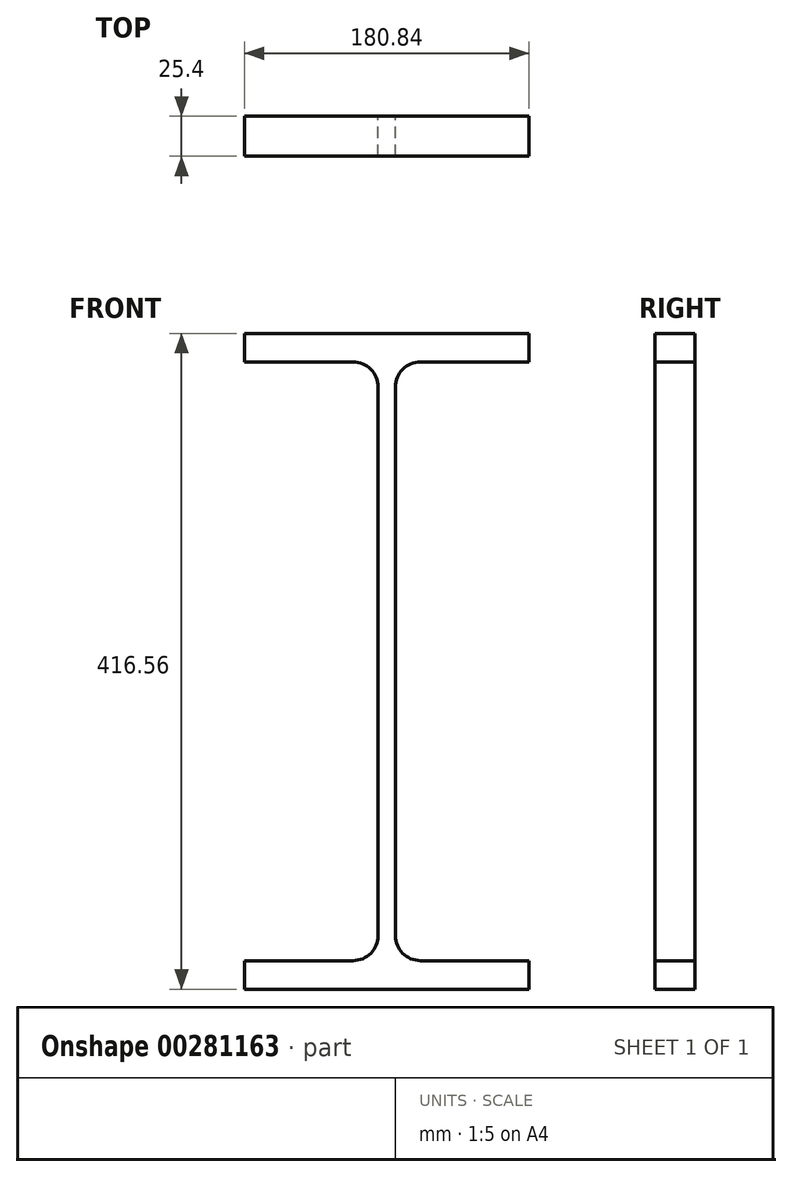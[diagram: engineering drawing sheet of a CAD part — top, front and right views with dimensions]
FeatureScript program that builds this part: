
annotation { "Feature Type Name" : "Feature", "Feature Type Description" : "" }
export const myFeature = defineFeature(function(context is Context, id is Id, definition is map)
    precondition{}
    {
        {
            var Q0;
            Q0=qCreatedBy(makeId("Front.planeOp"),FACE);
            var sketch = newSketch(context, id + "F0", { "sketchPlane" : qUnion([Q0])});
            skLineSegment(sketch, "E0.bottom", {"start": v(-90.42, 208.28) * mm, "end": v(90.42, 208.28) * mm});
            skLineSegment(sketch, "E0.top", {"start": v(-90.42, -208.28) * mm, "end": v(90.42, -208.28) * mm});
            skLineSegment(sketch, "E0.left", {"start": v(-90.42, 208.28) * mm, "end": v(-90.42, -208.28) * mm, "construction": true});
            skLineSegment(sketch, "E0.right", {"start": v(90.42, 208.28) * mm, "end": v(90.42, -208.28) * mm, "construction": true});
            skPoint(sketch, "E0.middle", {"position": v(0, 0) * mm});
            skLineSegment(sketch, "E1", {"start": v(-90.42, 208.28) * mm, "end": v(-90.42, 190.12) * mm});
            skLineSegment(sketch, "E2", {"start": v(-90.42, 190.12) * mm, "end": v(-21.34, 190.12) * mm});
            skLineSegment(sketch, "E3", {"start": v(-5.46, 174.24) * mm, "end": v(-5.46, -174.24) * mm});
            skLineSegment(sketch, "E4", {"start": v(-21.34, -190.12) * mm, "end": v(-90.42, -190.12) * mm});
            skLineSegment(sketch, "E5", {"start": v(-90.42, -190.12) * mm, "end": v(-90.42, -208.28) * mm});
            skLineSegment(sketch, "E6", {"start": v(90.42, 208.28) * mm, "end": v(90.42, 190.12) * mm});
            skLineSegment(sketch, "E7", {"start": v(90.42, 190.12) * mm, "end": v(21.34, 190.12) * mm});
            skLineSegment(sketch, "E8", {"start": v(5.46, 174.24) * mm, "end": v(5.46, -174.24) * mm});
            skLineSegment(sketch, "E9", {"start": v(21.34, -190.12) * mm, "end": v(90.42, -190.12) * mm});
            skLineSegment(sketch, "E10", {"start": v(90.42, -190.12) * mm, "end": v(90.42, -208.28) * mm});
            skPoint(sketch, "E11.visualSharp", {"position": v(-5.46, 190.12) * mm});
            skArc(sketch, "E11.filletArc", {"start": v(-5.46, 174.24) * mm, "mid": v(-10.11, 185.47) * mm, "end": v(-21.34, 190.12) * mm});
            skPoint(sketch, "E12.visualSharp", {"position": v(5.46, 190.12) * mm});
            skArc(sketch, "E12.filletArc", {"start": v(21.34, 190.12) * mm, "mid": v(10.11, 185.47) * mm, "end": v(5.46, 174.24) * mm});
            skPoint(sketch, "E13.visualSharp", {"position": v(5.46, -190.12) * mm});
            skArc(sketch, "E13.filletArc", {"start": v(5.46, -174.24) * mm, "mid": v(10.11, -185.47) * mm, "end": v(21.34, -190.12) * mm});
            skPoint(sketch, "E14.visualSharp", {"position": v(-5.46, -190.12) * mm});
            skArc(sketch, "E14.filletArc", {"start": v(-21.34, -190.12) * mm, "mid": v(-10.11, -185.47) * mm, "end": v(-5.46, -174.24) * mm});
            skSolve(sketch);
        }
        {
            var Q0;
            Q0 = qSketchRegion(id + "F0", true);
            extrude(context, id + "F1", {"entities" : qUnion([Q0]), "depth" : 25.4 * mm});
        }
    });
